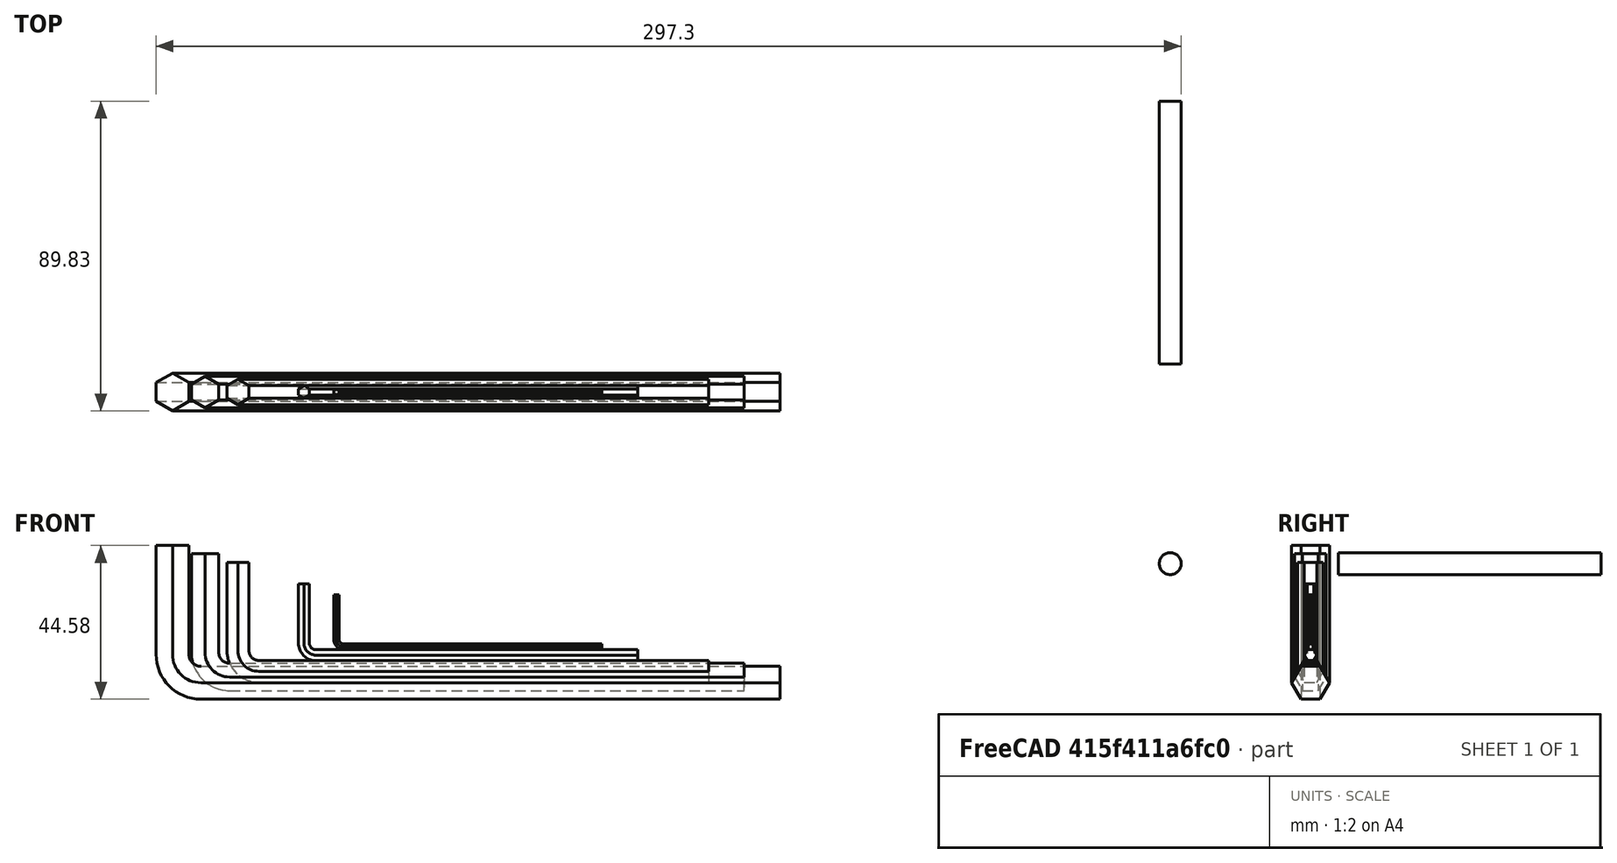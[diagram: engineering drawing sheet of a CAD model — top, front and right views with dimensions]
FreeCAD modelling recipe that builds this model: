
FCSTD DOCUMENT  (FreeCAD 0.20R)
Label: size_checker
License: All rights reserved
LicenseURL: http://en.wikipedia.org/wiki/All_rights_reserved
objects: Part::Feature×5, App::DocumentObjectGroup×2, Sketcher::SketchObject×1, PartDesign::Pad×1, PartDesign::Body×1, Mesh::Feature×1
note: 9 computed .brp shape members not serialized (recipe doc carries the construction recipe); baked Part::Feature solids carry a one-line shape summary decoded from their .brp

FEATURE [Sketcher::SketchObject] Sketch
  FullyConstrained = true
  MapMode = 5
  Placement = pos=(0,0,0) rot=(1,0,0;1.5708rad)
  Support = -> [XZ_Plane]
  sketch-geometry (1):
    g0: Circle CenterX=0 CenterY=0 CenterZ=0 NormalX=0 NormalY=0 NormalZ=1 AngleXU=0 Radius=3.175
  constraints (2):
    c: Coincident(g0,g-1)
    c: Diameter(g0) = 6.35
FEATURE [PartDesign::Pad] Pad
  Direction = (0,-1,2e-16)
  Length = 76.2
  Length2 = 10
  Placement = pos=(0,0,0) rot=(1,0,0;1.5708rad)
  Profile = -> Sketch
  ReferenceAxis = -> Sketch [N_Axis]
  Type = 0
FEATURE [PartDesign::Body] Body  label="1/4in drill"
  Group = -> [Sketch,Pad]
  Origin = -> Origin
  Placement = pos=(203.708,84.328,17.018) rot=(0,0,1;0rad)
  Tip = -> Pad
FEATURE [Mesh::Feature] drill_bit_organizer_imperial  label="drill_bit_organizer-imperial"
FEATURE [Part::Feature] Part__Feature  label="1-16_Hex L-Key"
  shape: bbox 77.79 x 1.833 x 15.81 mm, 20 faces (baked)
FEATURE [Part::Feature] __8_allen  label="1_8_allen"
  shape: bbox 98.43 x 3.666 x 22.23 mm, 20 faces (baked)
FEATURE [Part::Feature] __16_Hex_L_Key  label="3_16_Hex_L_Key"
  shape: bbox 139.7 x 7.332 x 34.8 mm, 20 faces (baked)
FEATURE [Part::Feature] __4_Hex_L_Key  label="1_4_Hex_L_Key"
  shape: bbox 160.3 x 9.165 x 39.69 mm, 20 faces (baked)
FEATURE [Part::Feature] __8_Hex_L_Key  label="3_8_Hex_L_Key"
  shape: bbox 181 x 11 x 44.58 mm, 20 faces (baked)
FEATURE [App::DocumentObjectGroup] Group  label="Allen_keys"
  Group = -> [Part__Feature,__8_allen,__16_Hex_L_Key,__4_Hex_L_Key,__8_Hex_L_Key]
FEATURE [App::DocumentObjectGroup] Group001  label="Drills"
  Group = -> [drill_bit_organizer_imperial,Body]
